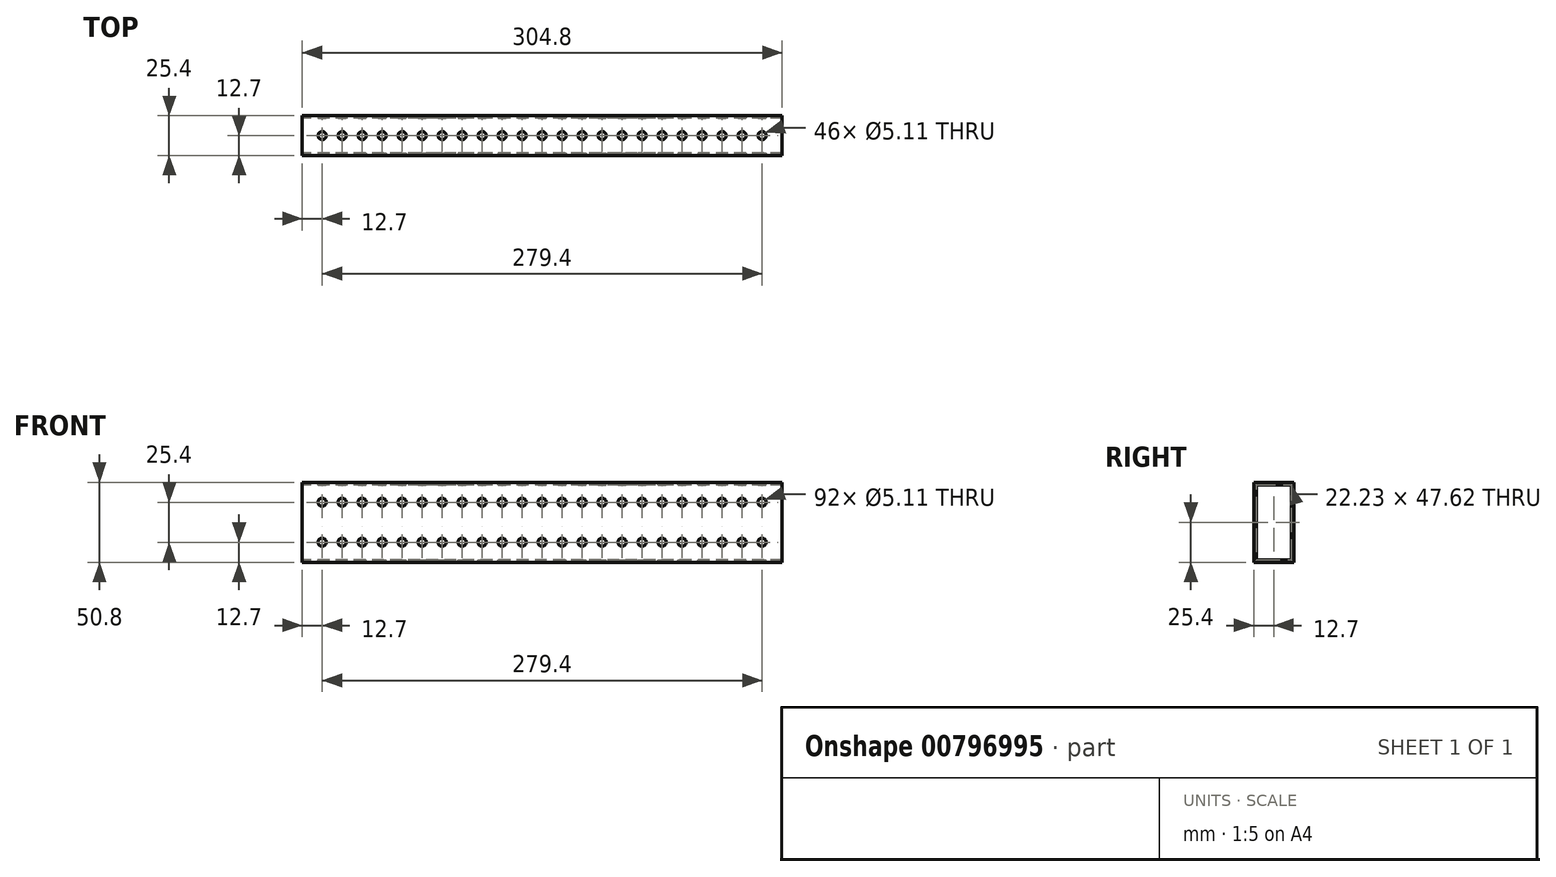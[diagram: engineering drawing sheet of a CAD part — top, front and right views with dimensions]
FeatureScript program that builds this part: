
annotation { "Feature Type Name" : "Feature", "Feature Type Description" : "" }
export const myFeature = defineFeature(function(context is Context, id is Id, definition is map)
    precondition{}
    {
        {
            var Q0;
            Q0=qCreatedBy(makeId("Right.planeOp"),FACE);
            var sketch = newSketch(context, id + "F0", { "sketchPlane" : qUnion([Q0])});
            skLineSegment(sketch, "E0.bottom", {"start": v(12.7, 25.4) * mm, "end": v(-12.7, 25.4) * mm});
            skLineSegment(sketch, "E0.top", {"start": v(12.7, -25.4) * mm, "end": v(-12.7, -25.4) * mm});
            skLineSegment(sketch, "E0.left", {"start": v(12.7, 25.4) * mm, "end": v(12.7, -25.4) * mm});
            skLineSegment(sketch, "E0.right", {"start": v(-12.7, 25.4) * mm, "end": v(-12.7, -25.4) * mm});
            skPoint(sketch, "E0.middle", {"position": v(0, 0) * mm});
            skLineSegment(sketch, "E1.0", {"start": v(-11.11, 23.81) * mm, "end": v(-11.11, -23.81) * mm});
            skLineSegment(sketch, "E1.1", {"start": v(11.11, 23.81) * mm, "end": v(-11.11, 23.81) * mm});
            skLineSegment(sketch, "E1.2", {"start": v(11.11, 23.81) * mm, "end": v(11.11, -23.81) * mm});
            skLineSegment(sketch, "E1.3", {"start": v(11.11, -23.81) * mm, "end": v(-11.11, -23.81) * mm});
            skSolve(sketch);
        }
        {
            var Q0;
            Q0=qSketchRegion(id+"F0",true);
            extrude(context, id + "F1", {"entities" : qUnion([Q0]), "depth" : 304.8 * mm, "offsetDistance" : 25.4 * mm});
        }
        {
            var Q0;
            Q0=makeQuery(id+"F1.opExtrude","SWEPT_FACE",FACE,{"disambiguationData":[OSD([sQuery(id+"F0.wireOp",EDGE,"E0.bottom")])]});
            var sketch = newSketch(context, id + "F2", { "sketchPlane" : qUnion([Q0])});
            skCircle(sketch, "E2", {"center": v(12.7, 0) * mm, "radius": 2.55 * mm});
            skCircle(sketch, "E3.1.0.0", {"center": v(25.4, 0) * mm, "radius": 2.55 * mm});
            skCircle(sketch, "E3.2.0.0", {"center": v(38.1, 0) * mm, "radius": 2.55 * mm});
            skCircle(sketch, "E3.3.0.0", {"center": v(50.8, 0) * mm, "radius": 2.55 * mm});
            skCircle(sketch, "E3.4.0.0", {"center": v(63.5, 0) * mm, "radius": 2.55 * mm});
            skCircle(sketch, "E3.5.0.0", {"center": v(76.2, 0) * mm, "radius": 2.55 * mm});
            skCircle(sketch, "E3.6.0.0", {"center": v(88.9, 0) * mm, "radius": 2.55 * mm});
            skCircle(sketch, "E3.7.0.0", {"center": v(101.6, 0) * mm, "radius": 2.55 * mm});
            skCircle(sketch, "E3.8.0.0", {"center": v(114.3, 0) * mm, "radius": 2.55 * mm});
            skCircle(sketch, "E3.9.0.0", {"center": v(127, 0) * mm, "radius": 2.55 * mm});
            skCircle(sketch, "E3.10.0.0", {"center": v(139.7, 0) * mm, "radius": 2.55 * mm});
            skCircle(sketch, "E3.11.0.0", {"center": v(152.4, 0) * mm, "radius": 2.55 * mm});
            skCircle(sketch, "E3.12.0.0", {"center": v(165.1, 0) * mm, "radius": 2.55 * mm});
            skCircle(sketch, "E3.13.0.0", {"center": v(177.8, 0) * mm, "radius": 2.55 * mm});
            skCircle(sketch, "E3.14.0.0", {"center": v(190.5, 0) * mm, "radius": 2.55 * mm});
            skCircle(sketch, "E3.15.0.0", {"center": v(203.2, 0) * mm, "radius": 2.55 * mm});
            skCircle(sketch, "E3.16.0.0", {"center": v(215.9, 0) * mm, "radius": 2.55 * mm});
            skCircle(sketch, "E3.17.0.0", {"center": v(228.6, 0) * mm, "radius": 2.55 * mm});
            skCircle(sketch, "E3.18.0.0", {"center": v(241.3, 0) * mm, "radius": 2.55 * mm});
            skCircle(sketch, "E3.19.0.0", {"center": v(254, 0) * mm, "radius": 2.55 * mm});
            skCircle(sketch, "E3.20.0.0", {"center": v(266.7, 0) * mm, "radius": 2.55 * mm});
            skCircle(sketch, "E3.21.0.0", {"center": v(279.4, 0) * mm, "radius": 2.55 * mm});
            skLineSegment(sketch, "E3.direction1", {"start": v(12.7, 0) * mm, "end": v(25.4, 0) * mm, "construction": true});
            skCircle(sketch, "E4.0.22.0", {"center": v(292.1, 0) * mm, "radius": 2.55 * mm});
            skSolve(sketch);
        }
        {
            var Q0;
            Q0=makeQuery(id+"F2.imprint","IMPRINT",FACE,{"disambiguationData":[TD([[makeQuery(id+"F2.imprint","IMPRINT",EDGE,{"derivedFrom":sQuery(id+"F2.wireOp",EDGE,"E2")}),1.0]])]});
            var Q1;
            Q1=makeQuery(id+"F2.imprint","IMPRINT",FACE,{"disambiguationData":[TD([[makeQuery(id+"F2.imprint","IMPRINT",EDGE,{"derivedFrom":sQuery(id+"F2.wireOp",EDGE,"E3.1.0.0")}),1.0]])]});
            var Q2;
            Q2=makeQuery(id+"F2.imprint","IMPRINT",FACE,{"disambiguationData":[TD([[makeQuery(id+"F2.imprint","IMPRINT",EDGE,{"derivedFrom":sQuery(id+"F2.wireOp",EDGE,"E3.2.0.0")}),1.0]])]});
            var Q3;
            Q3=makeQuery(id+"F2.imprint","IMPRINT",FACE,{"disambiguationData":[TD([[makeQuery(id+"F2.imprint","IMPRINT",EDGE,{"derivedFrom":sQuery(id+"F2.wireOp",EDGE,"E3.3.0.0")}),1.0]])]});
            var Q4;
            Q4=makeQuery(id+"F2.imprint","IMPRINT",FACE,{"disambiguationData":[TD([[makeQuery(id+"F2.imprint","IMPRINT",EDGE,{"derivedFrom":sQuery(id+"F2.wireOp",EDGE,"E3.4.0.0")}),1.0]])]});
            var Q5;
            Q5=makeQuery(id+"F2.imprint","IMPRINT",FACE,{"disambiguationData":[TD([[makeQuery(id+"F2.imprint","IMPRINT",EDGE,{"derivedFrom":sQuery(id+"F2.wireOp",EDGE,"E3.5.0.0")}),1.0]])]});
            var Q6;
            Q6=makeQuery(id+"F2.imprint","IMPRINT",FACE,{"disambiguationData":[TD([[makeQuery(id+"F2.imprint","IMPRINT",EDGE,{"derivedFrom":sQuery(id+"F2.wireOp",EDGE,"E3.6.0.0")}),1.0]])]});
            var Q7;
            Q7=makeQuery(id+"F2.imprint","IMPRINT",FACE,{"disambiguationData":[TD([[makeQuery(id+"F2.imprint","IMPRINT",EDGE,{"derivedFrom":sQuery(id+"F2.wireOp",EDGE,"E3.7.0.0")}),1.0]])]});
            var Q8;
            Q8=makeQuery(id+"F2.imprint","IMPRINT",FACE,{"disambiguationData":[TD([[makeQuery(id+"F2.imprint","IMPRINT",EDGE,{"derivedFrom":sQuery(id+"F2.wireOp",EDGE,"E3.8.0.0")}),1.0]])]});
            var Q9;
            Q9=makeQuery(id+"F2.imprint","IMPRINT",FACE,{"disambiguationData":[TD([[makeQuery(id+"F2.imprint","IMPRINT",EDGE,{"derivedFrom":sQuery(id+"F2.wireOp",EDGE,"E3.9.0.0")}),1.0]])]});
            var Q10;
            Q10=makeQuery(id+"F2.imprint","IMPRINT",FACE,{"disambiguationData":[TD([[makeQuery(id+"F2.imprint","IMPRINT",EDGE,{"derivedFrom":sQuery(id+"F2.wireOp",EDGE,"E3.10.0.0")}),1.0]])]});
            var Q11;
            Q11=makeQuery(id+"F2.imprint","IMPRINT",FACE,{"disambiguationData":[TD([[makeQuery(id+"F2.imprint","IMPRINT",EDGE,{"derivedFrom":sQuery(id+"F2.wireOp",EDGE,"E3.11.0.0")}),1.0]])]});
            var Q12;
            Q12=makeQuery(id+"F2.imprint","IMPRINT",FACE,{"disambiguationData":[TD([[makeQuery(id+"F2.imprint","IMPRINT",EDGE,{"derivedFrom":sQuery(id+"F2.wireOp",EDGE,"E3.12.0.0")}),1.0]])]});
            var Q13;
            Q13=makeQuery(id+"F2.imprint","IMPRINT",FACE,{"disambiguationData":[TD([[makeQuery(id+"F2.imprint","IMPRINT",EDGE,{"derivedFrom":sQuery(id+"F2.wireOp",EDGE,"E3.13.0.0")}),1.0]])]});
            var Q14;
            Q14=makeQuery(id+"F2.imprint","IMPRINT",FACE,{"disambiguationData":[TD([[makeQuery(id+"F2.imprint","IMPRINT",EDGE,{"derivedFrom":sQuery(id+"F2.wireOp",EDGE,"E3.14.0.0")}),1.0]])]});
            var Q15;
            Q15=makeQuery(id+"F2.imprint","IMPRINT",FACE,{"disambiguationData":[TD([[makeQuery(id+"F2.imprint","IMPRINT",EDGE,{"derivedFrom":sQuery(id+"F2.wireOp",EDGE,"E3.15.0.0")}),1.0]])]});
            var Q16;
            Q16=makeQuery(id+"F2.imprint","IMPRINT",FACE,{"disambiguationData":[TD([[makeQuery(id+"F2.imprint","IMPRINT",EDGE,{"derivedFrom":sQuery(id+"F2.wireOp",EDGE,"E3.16.0.0")}),1.0]])]});
            var Q17;
            Q17=makeQuery(id+"F2.imprint","IMPRINT",FACE,{"disambiguationData":[TD([[makeQuery(id+"F2.imprint","IMPRINT",EDGE,{"derivedFrom":sQuery(id+"F2.wireOp",EDGE,"E3.17.0.0")}),1.0]])]});
            var Q18;
            Q18=makeQuery(id+"F2.imprint","IMPRINT",FACE,{"disambiguationData":[TD([[makeQuery(id+"F2.imprint","IMPRINT",EDGE,{"derivedFrom":sQuery(id+"F2.wireOp",EDGE,"E3.18.0.0")}),1.0]])]});
            var Q19;
            Q19=makeQuery(id+"F2.imprint","IMPRINT",FACE,{"disambiguationData":[TD([[makeQuery(id+"F2.imprint","IMPRINT",EDGE,{"derivedFrom":sQuery(id+"F2.wireOp",EDGE,"E3.19.0.0")}),1.0]])]});
            var Q20;
            Q20=makeQuery(id+"F2.imprint","IMPRINT",FACE,{"disambiguationData":[TD([[makeQuery(id+"F2.imprint","IMPRINT",EDGE,{"derivedFrom":sQuery(id+"F2.wireOp",EDGE,"E3.20.0.0")}),1.0]])]});
            var Q21;
            Q21=makeQuery(id+"F2.imprint","IMPRINT",FACE,{"disambiguationData":[TD([[makeQuery(id+"F2.imprint","IMPRINT",EDGE,{"derivedFrom":sQuery(id+"F2.wireOp",EDGE,"E3.21.0.0")}),1.0]])]});
            var Q22;
            Q22=makeQuery(id+"F2.imprint","IMPRINT",FACE,{"disambiguationData":[TD([[makeQuery(id+"F2.imprint","IMPRINT",EDGE,{"derivedFrom":sQuery(id+"F2.wireOp",EDGE,"E4.0.22.0")}),1.0]])]});
            var Q23;
            Q23=makeQuery(id+"F2.imprint","IMPRINT",FACE,{"disambiguationData":[TD([[makeQuery(id+"F2.imprint","IMPRINT",EDGE,{"derivedFrom":sQuery(id+"F2.wireOp",EDGE,"E4.0.23.0")}),1.0]])]});
            var Q24;
            Q24=makeQuery(id+"F2.imprint","IMPRINT",FACE,{"disambiguationData":[TD([[makeQuery(id+"F2.imprint","IMPRINT",EDGE,{"derivedFrom":sQuery(id+"F2.wireOp",EDGE,"E4.0.24.0")}),1.0]])]});
            var Q25;
            Q25=makeQuery(id+"F2.imprint","IMPRINT",FACE,{"disambiguationData":[TD([[makeQuery(id+"F2.imprint","IMPRINT",EDGE,{"derivedFrom":sQuery(id+"F2.wireOp",EDGE,"E4.0.25.0")}),1.0]])]});
            var Q26;
            Q26=makeQuery(id+"F2.imprint","IMPRINT",FACE,{"disambiguationData":[TD([[makeQuery(id+"F2.imprint","IMPRINT",EDGE,{"derivedFrom":sQuery(id+"F2.wireOp",EDGE,"E4.0.26.0")}),1.0]])]});
            var Q27;
            Q27=makeQuery(id+"F2.imprint","IMPRINT",FACE,{"disambiguationData":[TD([[makeQuery(id+"F2.imprint","IMPRINT",EDGE,{"derivedFrom":sQuery(id+"F2.wireOp",EDGE,"E4.0.27.0")}),1.0]])]});
            var Q28;
            Q28=makeQuery(id+"F2.imprint","IMPRINT",FACE,{"disambiguationData":[TD([[makeQuery(id+"F2.imprint","IMPRINT",EDGE,{"derivedFrom":sQuery(id+"F2.wireOp",EDGE,"E4.0.28.0")}),1.0]])]});
            var Q29;
            Q29=makeQuery(id+"F2.imprint","IMPRINT",FACE,{"disambiguationData":[TD([[makeQuery(id+"F2.imprint","IMPRINT",EDGE,{"derivedFrom":sQuery(id+"F2.wireOp",EDGE,"E4.0.29.0")}),1.0]])]});
            var Q30;
            Q30=makeQuery(id+"F2.imprint","IMPRINT",FACE,{"disambiguationData":[TD([[makeQuery(id+"F2.imprint","IMPRINT",EDGE,{"derivedFrom":sQuery(id+"F2.wireOp",EDGE,"f3a4a80a-b25e-401b-99ed-effaa224f588.0.30.0")}),1.0]])]});
            extrude(context, id + "F3", {"entities" : qUnion([Q0, Q1, Q2, Q3, Q4, Q5, Q6, Q7, Q8, Q9, Q10, Q11, Q12, Q13, Q14, Q15, Q16, Q17, Q18, Q19, Q20, Q21, Q22, Q23, Q24, Q25, Q26, Q27, Q28, Q29, Q30]), "operationType" : NewBodyOperationType.REMOVE, "oppositeDirection" : true, "depth" : 254 * mm, "offsetDistance" : 25.4 * mm});
        }
        {
            var Q0;
            Q0=makeQuery(id+"F1.opExtrude","SWEPT_FACE",FACE,{"disambiguationData":[OSD([sQuery(id+"F0.wireOp",EDGE,"E0.right")])]});
            var sketch = newSketch(context, id + "F4", { "sketchPlane" : qUnion([Q0])});
            skCircle(sketch, "E5", {"center": v(12.7, 12.7) * mm, "radius": 2.55 * mm});
            skCircle(sketch, "E6.0.1.0", {"center": v(12.7, -12.7) * mm, "radius": 2.55 * mm});
            skCircle(sketch, "E6.1.0.0", {"center": v(25.4, 12.7) * mm, "radius": 2.55 * mm});
            skCircle(sketch, "E6.1.1.0", {"center": v(25.4, -12.7) * mm, "radius": 2.55 * mm});
            skCircle(sketch, "E6.2.0.0", {"center": v(38.1, 12.7) * mm, "radius": 2.55 * mm});
            skCircle(sketch, "E6.2.1.0", {"center": v(38.1, -12.7) * mm, "radius": 2.55 * mm});
            skCircle(sketch, "E6.3.0.0", {"center": v(50.8, 12.7) * mm, "radius": 2.55 * mm});
            skCircle(sketch, "E6.3.1.0", {"center": v(50.8, -12.7) * mm, "radius": 2.55 * mm});
            skCircle(sketch, "E6.4.0.0", {"center": v(63.5, 12.7) * mm, "radius": 2.55 * mm});
            skCircle(sketch, "E6.4.1.0", {"center": v(63.5, -12.7) * mm, "radius": 2.55 * mm});
            skCircle(sketch, "E6.5.0.0", {"center": v(76.2, 12.7) * mm, "radius": 2.55 * mm});
            skCircle(sketch, "E6.5.1.0", {"center": v(76.2, -12.7) * mm, "radius": 2.55 * mm});
            skCircle(sketch, "E6.6.0.0", {"center": v(88.9, 12.7) * mm, "radius": 2.55 * mm});
            skCircle(sketch, "E6.6.1.0", {"center": v(88.9, -12.7) * mm, "radius": 2.55 * mm});
            skCircle(sketch, "E6.7.0.0", {"center": v(101.6, 12.7) * mm, "radius": 2.55 * mm});
            skCircle(sketch, "E6.7.1.0", {"center": v(101.6, -12.7) * mm, "radius": 2.55 * mm});
            skCircle(sketch, "E6.8.0.0", {"center": v(114.3, 12.7) * mm, "radius": 2.55 * mm});
            skCircle(sketch, "E6.8.1.0", {"center": v(114.3, -12.7) * mm, "radius": 2.55 * mm});
            skCircle(sketch, "E6.9.0.0", {"center": v(127, 12.7) * mm, "radius": 2.55 * mm});
            skCircle(sketch, "E6.9.1.0", {"center": v(127, -12.7) * mm, "radius": 2.55 * mm});
            skCircle(sketch, "E6.10.0.0", {"center": v(139.7, 12.7) * mm, "radius": 2.55 * mm});
            skCircle(sketch, "E6.10.1.0", {"center": v(139.7, -12.7) * mm, "radius": 2.55 * mm});
            skCircle(sketch, "E6.11.0.0", {"center": v(152.4, 12.7) * mm, "radius": 2.55 * mm});
            skCircle(sketch, "E6.11.1.0", {"center": v(152.4, -12.7) * mm, "radius": 2.55 * mm});
            skCircle(sketch, "E6.12.0.0", {"center": v(165.1, 12.7) * mm, "radius": 2.55 * mm});
            skCircle(sketch, "E6.12.1.0", {"center": v(165.1, -12.7) * mm, "radius": 2.55 * mm});
            skCircle(sketch, "E6.13.0.0", {"center": v(177.8, 12.7) * mm, "radius": 2.55 * mm});
            skCircle(sketch, "E6.13.1.0", {"center": v(177.8, -12.7) * mm, "radius": 2.55 * mm});
            skCircle(sketch, "E6.14.0.0", {"center": v(190.5, 12.7) * mm, "radius": 2.55 * mm});
            skCircle(sketch, "E6.14.1.0", {"center": v(190.5, -12.7) * mm, "radius": 2.55 * mm});
            skCircle(sketch, "E6.15.0.0", {"center": v(203.2, 12.7) * mm, "radius": 2.55 * mm});
            skCircle(sketch, "E6.15.1.0", {"center": v(203.2, -12.7) * mm, "radius": 2.55 * mm});
            skCircle(sketch, "E6.16.0.0", {"center": v(215.9, 12.7) * mm, "radius": 2.55 * mm});
            skCircle(sketch, "E6.16.1.0", {"center": v(215.9, -12.7) * mm, "radius": 2.55 * mm});
            skCircle(sketch, "E6.17.0.0", {"center": v(228.6, 12.7) * mm, "radius": 2.55 * mm});
            skCircle(sketch, "E6.17.1.0", {"center": v(228.6, -12.7) * mm, "radius": 2.55 * mm});
            skCircle(sketch, "E6.18.0.0", {"center": v(241.3, 12.7) * mm, "radius": 2.55 * mm});
            skCircle(sketch, "E6.18.1.0", {"center": v(241.3, -12.7) * mm, "radius": 2.55 * mm});
            skCircle(sketch, "E6.19.0.0", {"center": v(254, 12.7) * mm, "radius": 2.55 * mm});
            skCircle(sketch, "E6.19.1.0", {"center": v(254, -12.7) * mm, "radius": 2.55 * mm});
            skCircle(sketch, "E6.20.0.0", {"center": v(266.7, 12.7) * mm, "radius": 2.55 * mm});
            skCircle(sketch, "E6.20.1.0", {"center": v(266.7, -12.7) * mm, "radius": 2.55 * mm});
            skCircle(sketch, "E6.21.0.0", {"center": v(279.4, 12.7) * mm, "radius": 2.55 * mm});
            skCircle(sketch, "E6.21.1.0", {"center": v(279.4, -12.7) * mm, "radius": 2.55 * mm});
            skCircle(sketch, "E6.22.0.0", {"center": v(292.1, 12.7) * mm, "radius": 2.55 * mm});
            skCircle(sketch, "E6.22.1.0", {"center": v(292.1, -12.7) * mm, "radius": 2.55 * mm});
            skLineSegment(sketch, "E6.direction1", {"start": v(12.7, 12.7) * mm, "end": v(25.4, 12.7) * mm, "construction": true});
            skLineSegment(sketch, "E6.direction2", {"start": v(12.7, 12.7) * mm, "end": v(12.7, -12.7) * mm, "construction": true});
            skLineSegment(sketch, "E7.bottom", {"start": v(304.8, 25.4) * mm, "end": v(0, 25.4) * mm});
            skLineSegment(sketch, "E7.top", {"start": v(304.8, -25.4) * mm, "end": v(0, -25.4) * mm});
            skLineSegment(sketch, "E7.left", {"start": v(304.8, 25.4) * mm, "end": v(304.8, -25.4) * mm});
            skLineSegment(sketch, "E7.right", {"start": v(0, 25.4) * mm, "end": v(0, -25.4) * mm});
            skSolve(sketch);
        }
        {
            var Q0;
            Q0=makeQuery(id+"F4.imprint","IMPRINT",FACE,{"disambiguationData":[TD([[makeQuery(id+"F4.imprint","IMPRINT",EDGE,{"derivedFrom":sQuery(id+"F4.wireOp",EDGE,"E6.8.0.0")}),1.0]])]});
            var Q1;
            Q1=makeQuery(id+"F4.imprint","IMPRINT",FACE,{"disambiguationData":[TD([[makeQuery(id+"F4.imprint","IMPRINT",EDGE,{"derivedFrom":sQuery(id+"F4.wireOp",EDGE,"E6.13.0.0")}),1.0]])]});
            var Q2;
            Q2=makeQuery(id+"F4.imprint","IMPRINT",FACE,{"disambiguationData":[TD([[makeQuery(id+"F4.imprint","IMPRINT",EDGE,{"derivedFrom":sQuery(id+"F4.wireOp",EDGE,"E6.1.1.0")}),1.0]])]});
            var Q3;
            Q3=makeQuery(id+"F4.imprint","IMPRINT",FACE,{"disambiguationData":[TD([[makeQuery(id+"F4.imprint","IMPRINT",EDGE,{"derivedFrom":sQuery(id+"F4.wireOp",EDGE,"E6.27.1.0")}),1.0]])]});
            var Q4;
            Q4=makeQuery(id+"F4.imprint","IMPRINT",FACE,{"disambiguationData":[TD([[makeQuery(id+"F4.imprint","IMPRINT",EDGE,{"derivedFrom":sQuery(id+"F4.wireOp",EDGE,"E5")}),1.0]])]});
            var Q5;
            Q5=makeQuery(id+"F4.imprint","IMPRINT",FACE,{"disambiguationData":[TD([[makeQuery(id+"F4.imprint","IMPRINT",EDGE,{"derivedFrom":sQuery(id+"F4.wireOp",EDGE,"E6.26.0.0")}),1.0]])]});
            var Q6;
            Q6=makeQuery(id+"F4.imprint","IMPRINT",FACE,{"disambiguationData":[TD([[makeQuery(id+"F4.imprint","IMPRINT",EDGE,{"derivedFrom":sQuery(id+"F4.wireOp",EDGE,"E6.18.1.0")}),1.0]])]});
            var Q7;
            Q7=makeQuery(id+"F4.imprint","IMPRINT",FACE,{"disambiguationData":[TD([[makeQuery(id+"F4.imprint","IMPRINT",EDGE,{"derivedFrom":sQuery(id+"F4.wireOp",EDGE,"E6.24.1.0")}),1.0]])]});
            var Q8;
            Q8=makeQuery(id+"F4.imprint","IMPRINT",FACE,{"disambiguationData":[TD([[makeQuery(id+"F4.imprint","IMPRINT",EDGE,{"derivedFrom":sQuery(id+"F4.wireOp",EDGE,"E6.28.0.0")}),1.0]])]});
            var Q9;
            Q9=makeQuery(id+"F4.imprint","IMPRINT",FACE,{"disambiguationData":[TD([[makeQuery(id+"F4.imprint","IMPRINT",EDGE,{"derivedFrom":sQuery(id+"F4.wireOp",EDGE,"E6.19.1.0")}),1.0]])]});
            var Q10;
            Q10=makeQuery(id+"F4.imprint","IMPRINT",FACE,{"disambiguationData":[TD([[makeQuery(id+"F4.imprint","IMPRINT",EDGE,{"derivedFrom":sQuery(id+"F4.wireOp",EDGE,"E6.10.0.0")}),1.0]])]});
            var Q11;
            Q11=makeQuery(id+"F4.imprint","IMPRINT",FACE,{"disambiguationData":[TD([[makeQuery(id+"F4.imprint","IMPRINT",EDGE,{"derivedFrom":sQuery(id+"F4.wireOp",EDGE,"E6.2.1.0")}),1.0]])]});
            var Q12;
            Q12=makeQuery(id+"F4.imprint","IMPRINT",FACE,{"disambiguationData":[TD([[makeQuery(id+"F4.imprint","IMPRINT",EDGE,{"derivedFrom":sQuery(id+"F4.wireOp",EDGE,"E6.16.0.0")}),1.0]])]});
            var Q13;
            Q13=makeQuery(id+"F4.imprint","IMPRINT",FACE,{"disambiguationData":[TD([[makeQuery(id+"F4.imprint","IMPRINT",EDGE,{"derivedFrom":sQuery(id+"F4.wireOp",EDGE,"E6.25.0.0")}),1.0]])]});
            var Q14;
            Q14=makeQuery(id+"F4.imprint","IMPRINT",FACE,{"disambiguationData":[TD([[makeQuery(id+"F4.imprint","IMPRINT",EDGE,{"derivedFrom":sQuery(id+"F4.wireOp",EDGE,"E6.5.0.0")}),1.0]])]});
            var Q15;
            Q15=makeQuery(id+"F4.imprint","IMPRINT",FACE,{"disambiguationData":[TD([[makeQuery(id+"F4.imprint","IMPRINT",EDGE,{"derivedFrom":sQuery(id+"F4.wireOp",EDGE,"E6.18.0.0")}),1.0]])]});
            var Q16;
            Q16=makeQuery(id+"F4.imprint","IMPRINT",FACE,{"disambiguationData":[TD([[makeQuery(id+"F4.imprint","IMPRINT",EDGE,{"derivedFrom":sQuery(id+"F4.wireOp",EDGE,"E6.22.0.0")}),1.0]])]});
            var Q17;
            Q17=makeQuery(id+"F4.imprint","IMPRINT",FACE,{"disambiguationData":[TD([[makeQuery(id+"F4.imprint","IMPRINT",EDGE,{"derivedFrom":sQuery(id+"F4.wireOp",EDGE,"E6.24.0.0")}),1.0]])]});
            var Q18;
            Q18=makeQuery(id+"F4.imprint","IMPRINT",FACE,{"disambiguationData":[TD([[makeQuery(id+"F4.imprint","IMPRINT",EDGE,{"derivedFrom":sQuery(id+"F4.wireOp",EDGE,"E6.9.0.0")}),1.0]])]});
            var Q19;
            Q19=makeQuery(id+"F4.imprint","IMPRINT",FACE,{"disambiguationData":[TD([[makeQuery(id+"F4.imprint","IMPRINT",EDGE,{"derivedFrom":sQuery(id+"F4.wireOp",EDGE,"E6.7.1.0")}),1.0]])]});
            var Q20;
            Q20=makeQuery(id+"F4.imprint","IMPRINT",FACE,{"disambiguationData":[TD([[makeQuery(id+"F4.imprint","IMPRINT",EDGE,{"derivedFrom":sQuery(id+"F4.wireOp",EDGE,"E6.21.0.0")}),1.0]])]});
            var Q21;
            Q21=makeQuery(id+"F4.imprint","IMPRINT",FACE,{"disambiguationData":[TD([[makeQuery(id+"F4.imprint","IMPRINT",EDGE,{"derivedFrom":sQuery(id+"F4.wireOp",EDGE,"E6.25.1.0")}),1.0]])]});
            var Q22;
            Q22=makeQuery(id+"F4.imprint","IMPRINT",FACE,{"disambiguationData":[TD([[makeQuery(id+"F4.imprint","IMPRINT",EDGE,{"derivedFrom":sQuery(id+"F4.wireOp",EDGE,"E6.12.1.0")}),1.0]])]});
            var Q23;
            Q23=makeQuery(id+"F4.imprint","IMPRINT",FACE,{"disambiguationData":[TD([[makeQuery(id+"F4.imprint","IMPRINT",EDGE,{"derivedFrom":sQuery(id+"F4.wireOp",EDGE,"E6.27.0.0")}),1.0]])]});
            var Q24;
            Q24=makeQuery(id+"F4.imprint","IMPRINT",FACE,{"disambiguationData":[TD([[makeQuery(id+"F4.imprint","IMPRINT",EDGE,{"derivedFrom":sQuery(id+"F4.wireOp",EDGE,"E6.28.1.0")}),1.0]])]});
            var Q25;
            Q25=makeQuery(id+"F4.imprint","IMPRINT",FACE,{"disambiguationData":[TD([[makeQuery(id+"F4.imprint","IMPRINT",EDGE,{"derivedFrom":sQuery(id+"F4.wireOp",EDGE,"E6.12.0.0")}),1.0]])]});
            var Q26;
            Q26=makeQuery(id+"F4.imprint","IMPRINT",FACE,{"disambiguationData":[TD([[makeQuery(id+"F4.imprint","IMPRINT",EDGE,{"derivedFrom":sQuery(id+"F4.wireOp",EDGE,"E6.11.1.0")}),1.0]])]});
            var Q27;
            Q27=makeQuery(id+"F4.imprint","IMPRINT",FACE,{"disambiguationData":[TD([[makeQuery(id+"F4.imprint","IMPRINT",EDGE,{"derivedFrom":sQuery(id+"F4.wireOp",EDGE,"E6.20.0.0")}),1.0]])]});
            var Q28;
            Q28=makeQuery(id+"F4.imprint","IMPRINT",FACE,{"disambiguationData":[TD([[makeQuery(id+"F4.imprint","IMPRINT",EDGE,{"derivedFrom":sQuery(id+"F4.wireOp",EDGE,"E6.4.1.0")}),1.0]])]});
            var Q29;
            Q29=makeQuery(id+"F4.imprint","IMPRINT",FACE,{"disambiguationData":[TD([[makeQuery(id+"F4.imprint","IMPRINT",EDGE,{"derivedFrom":sQuery(id+"F4.wireOp",EDGE,"E6.30.0.0")}),1.0]])]});
            var Q30;
            Q30=makeQuery(id+"F4.imprint","IMPRINT",FACE,{"disambiguationData":[TD([[makeQuery(id+"F4.imprint","IMPRINT",EDGE,{"derivedFrom":sQuery(id+"F4.wireOp",EDGE,"E6.16.1.0")}),1.0]])]});
            var Q31;
            Q31=makeQuery(id+"F4.imprint","IMPRINT",FACE,{"disambiguationData":[TD([[makeQuery(id+"F4.imprint","IMPRINT",EDGE,{"derivedFrom":sQuery(id+"F4.wireOp",EDGE,"E6.13.1.0")}),1.0]])]});
            var Q32;
            Q32=makeQuery(id+"F4.imprint","IMPRINT",FACE,{"disambiguationData":[TD([[makeQuery(id+"F4.imprint","IMPRINT",EDGE,{"derivedFrom":sQuery(id+"F4.wireOp",EDGE,"E6.19.0.0")}),1.0]])]});
            var Q33;
            Q33=makeQuery(id+"F4.imprint","IMPRINT",FACE,{"disambiguationData":[TD([[makeQuery(id+"F4.imprint","IMPRINT",EDGE,{"derivedFrom":sQuery(id+"F4.wireOp",EDGE,"E6.17.0.0")}),1.0]])]});
            var Q34;
            Q34=makeQuery(id+"F4.imprint","IMPRINT",FACE,{"disambiguationData":[TD([[makeQuery(id+"F4.imprint","IMPRINT",EDGE,{"derivedFrom":sQuery(id+"F4.wireOp",EDGE,"E6.11.0.0")}),1.0]])]});
            var Q35;
            Q35=makeQuery(id+"F4.imprint","IMPRINT",FACE,{"disambiguationData":[TD([[makeQuery(id+"F4.imprint","IMPRINT",EDGE,{"derivedFrom":sQuery(id+"F4.wireOp",EDGE,"E6.29.0.0")}),1.0]])]});
            var Q36;
            Q36=makeQuery(id+"F4.imprint","IMPRINT",FACE,{"disambiguationData":[TD([[makeQuery(id+"F4.imprint","IMPRINT",EDGE,{"derivedFrom":sQuery(id+"F4.wireOp",EDGE,"E6.23.0.0")}),1.0]])]});
            var Q37;
            Q37=makeQuery(id+"F4.imprint","IMPRINT",FACE,{"disambiguationData":[TD([[makeQuery(id+"F4.imprint","IMPRINT",EDGE,{"derivedFrom":sQuery(id+"F4.wireOp",EDGE,"E6.2.0.0")}),1.0]])]});
            var Q38;
            Q38=makeQuery(id+"F4.imprint","IMPRINT",FACE,{"disambiguationData":[TD([[makeQuery(id+"F4.imprint","IMPRINT",EDGE,{"derivedFrom":sQuery(id+"F4.wireOp",EDGE,"E6.0.1.0")}),1.0]])]});
            var Q39;
            Q39=makeQuery(id+"F4.imprint","IMPRINT",FACE,{"disambiguationData":[TD([[makeQuery(id+"F4.imprint","IMPRINT",EDGE,{"derivedFrom":sQuery(id+"F4.wireOp",EDGE,"E6.10.1.0")}),1.0]])]});
            var Q40;
            Q40=makeQuery(id+"F4.imprint","IMPRINT",FACE,{"disambiguationData":[TD([[makeQuery(id+"F4.imprint","IMPRINT",EDGE,{"derivedFrom":sQuery(id+"F4.wireOp",EDGE,"E6.20.1.0")}),1.0]])]});
            var Q41;
            Q41=makeQuery(id+"F4.imprint","IMPRINT",FACE,{"disambiguationData":[TD([[makeQuery(id+"F4.imprint","IMPRINT",EDGE,{"derivedFrom":sQuery(id+"F4.wireOp",EDGE,"E6.21.1.0")}),1.0]])]});
            var Q42;
            Q42=makeQuery(id+"F4.imprint","IMPRINT",FACE,{"disambiguationData":[TD([[makeQuery(id+"F4.imprint","IMPRINT",EDGE,{"derivedFrom":sQuery(id+"F4.wireOp",EDGE,"E6.9.1.0")}),1.0]])]});
            var Q43;
            Q43=makeQuery(id+"F4.imprint","IMPRINT",FACE,{"disambiguationData":[TD([[makeQuery(id+"F4.imprint","IMPRINT",EDGE,{"derivedFrom":sQuery(id+"F4.wireOp",EDGE,"E6.1.0.0")}),1.0]])]});
            var Q44;
            Q44=makeQuery(id+"F4.imprint","IMPRINT",FACE,{"disambiguationData":[TD([[makeQuery(id+"F4.imprint","IMPRINT",EDGE,{"derivedFrom":sQuery(id+"F4.wireOp",EDGE,"E6.26.1.0")}),1.0]])]});
            var Q45;
            Q45=makeQuery(id+"F4.imprint","IMPRINT",FACE,{"disambiguationData":[TD([[makeQuery(id+"F4.imprint","IMPRINT",EDGE,{"derivedFrom":sQuery(id+"F4.wireOp",EDGE,"E6.14.1.0")}),1.0]])]});
            var Q46;
            Q46=makeQuery(id+"F4.imprint","IMPRINT",FACE,{"disambiguationData":[TD([[makeQuery(id+"F4.imprint","IMPRINT",EDGE,{"derivedFrom":sQuery(id+"F4.wireOp",EDGE,"E6.3.0.0")}),1.0]])]});
            var Q47;
            Q47=makeQuery(id+"F4.imprint","IMPRINT",FACE,{"disambiguationData":[TD([[makeQuery(id+"F4.imprint","IMPRINT",EDGE,{"derivedFrom":sQuery(id+"F4.wireOp",EDGE,"E6.7.0.0")}),1.0]])]});
            var Q48;
            Q48=makeQuery(id+"F4.imprint","IMPRINT",FACE,{"disambiguationData":[TD([[makeQuery(id+"F4.imprint","IMPRINT",EDGE,{"derivedFrom":sQuery(id+"F4.wireOp",EDGE,"E6.17.1.0")}),1.0]])]});
            var Q49;
            Q49=makeQuery(id+"F4.imprint","IMPRINT",FACE,{"disambiguationData":[TD([[makeQuery(id+"F4.imprint","IMPRINT",EDGE,{"derivedFrom":sQuery(id+"F4.wireOp",EDGE,"E6.3.1.0")}),1.0]])]});
            var Q50;
            Q50=makeQuery(id+"F4.imprint","IMPRINT",FACE,{"disambiguationData":[TD([[makeQuery(id+"F4.imprint","IMPRINT",EDGE,{"derivedFrom":sQuery(id+"F4.wireOp",EDGE,"E6.29.1.0")}),1.0]])]});
            var Q51;
            Q51=makeQuery(id+"F4.imprint","IMPRINT",FACE,{"disambiguationData":[TD([[makeQuery(id+"F4.imprint","IMPRINT",EDGE,{"derivedFrom":sQuery(id+"F4.wireOp",EDGE,"E6.6.0.0")}),1.0]])]});
            var Q52;
            Q52=makeQuery(id+"F4.imprint","IMPRINT",FACE,{"disambiguationData":[TD([[makeQuery(id+"F4.imprint","IMPRINT",EDGE,{"derivedFrom":sQuery(id+"F4.wireOp",EDGE,"E6.14.0.0")}),1.0]])]});
            var Q53;
            Q53=makeQuery(id+"F4.imprint","IMPRINT",FACE,{"disambiguationData":[TD([[makeQuery(id+"F4.imprint","IMPRINT",EDGE,{"derivedFrom":sQuery(id+"F4.wireOp",EDGE,"E6.8.1.0")}),1.0]])]});
            var Q54;
            Q54=makeQuery(id+"F4.imprint","IMPRINT",FACE,{"disambiguationData":[TD([[makeQuery(id+"F4.imprint","IMPRINT",EDGE,{"derivedFrom":sQuery(id+"F4.wireOp",EDGE,"E6.23.1.0")}),1.0]])]});
            var Q55;
            Q55=makeQuery(id+"F4.imprint","IMPRINT",FACE,{"disambiguationData":[TD([[makeQuery(id+"F4.imprint","IMPRINT",EDGE,{"derivedFrom":sQuery(id+"F4.wireOp",EDGE,"E6.6.1.0")}),1.0]])]});
            var Q56;
            Q56=makeQuery(id+"F4.imprint","IMPRINT",FACE,{"disambiguationData":[TD([[makeQuery(id+"F4.imprint","IMPRINT",EDGE,{"derivedFrom":sQuery(id+"F4.wireOp",EDGE,"E6.15.1.0")}),1.0]])]});
            var Q57;
            Q57=makeQuery(id+"F4.imprint","IMPRINT",FACE,{"disambiguationData":[TD([[makeQuery(id+"F4.imprint","IMPRINT",EDGE,{"derivedFrom":sQuery(id+"F4.wireOp",EDGE,"E6.5.1.0")}),1.0]])]});
            var Q58;
            Q58=makeQuery(id+"F4.imprint","IMPRINT",FACE,{"disambiguationData":[TD([[makeQuery(id+"F4.imprint","IMPRINT",EDGE,{"derivedFrom":sQuery(id+"F4.wireOp",EDGE,"E6.4.0.0")}),1.0]])]});
            var Q59;
            Q59=makeQuery(id+"F4.imprint","IMPRINT",FACE,{"disambiguationData":[TD([[makeQuery(id+"F4.imprint","IMPRINT",EDGE,{"derivedFrom":sQuery(id+"F4.wireOp",EDGE,"E6.15.0.0")}),1.0]])]});
            var Q60;
            Q60=makeQuery(id+"F4.imprint","IMPRINT",FACE,{"disambiguationData":[TD([[makeQuery(id+"F4.imprint","IMPRINT",EDGE,{"derivedFrom":sQuery(id+"F4.wireOp",EDGE,"E6.30.1.0")}),1.0]])]});
            var Q61;
            Q61=makeQuery(id+"F4.imprint","IMPRINT",FACE,{"disambiguationData":[TD([[makeQuery(id+"F4.imprint","IMPRINT",EDGE,{"derivedFrom":sQuery(id+"F4.wireOp",EDGE,"E6.22.1.0")}),1.0]])]});
            extrude(context, id + "F5", {"entities" : qUnion([Q0, Q1, Q2, Q3, Q4, Q5, Q6, Q7, Q8, Q9, Q10, Q11, Q12, Q13, Q14, Q15, Q16, Q17, Q18, Q19, Q20, Q21, Q22, Q23, Q24, Q25, Q26, Q27, Q28, Q29, Q30, Q31, Q32, Q33, Q34, Q35, Q36, Q37, Q38, Q39, Q40, Q41, Q42, Q43, Q44, Q45, Q46, Q47, Q48, Q49, Q50, Q51, Q52, Q53, Q54, Q55, Q56, Q57, Q58, Q59, Q60, Q61]), "operationType" : NewBodyOperationType.REMOVE, "oppositeDirection" : true, "depth" : 76.2 * mm, "offsetDistance" : 25.4 * mm});
        }
    });
